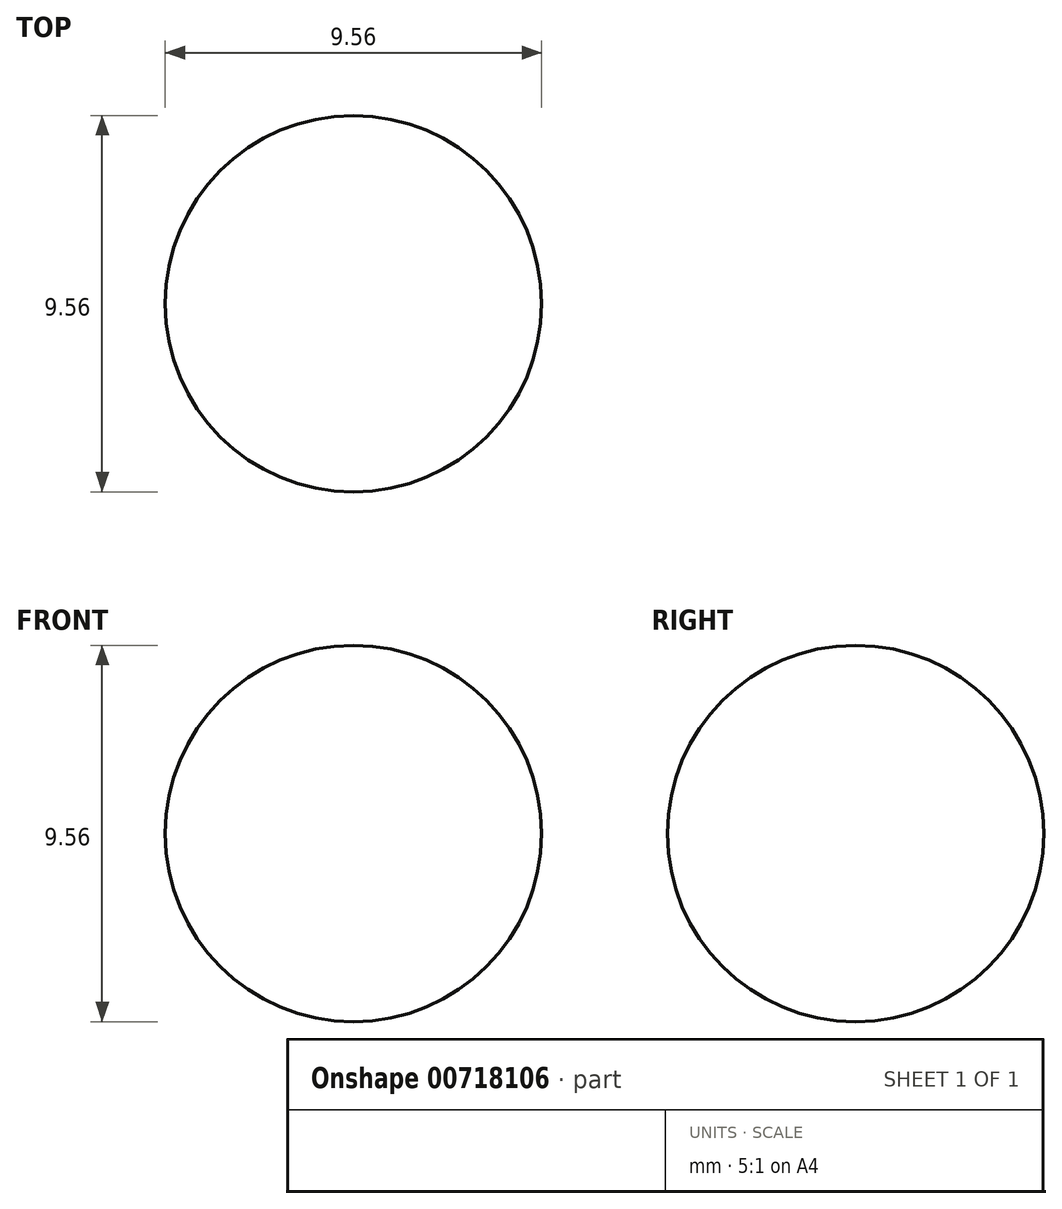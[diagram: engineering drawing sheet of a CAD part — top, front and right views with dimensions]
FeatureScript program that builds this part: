
annotation { "Feature Type Name" : "Feature", "Feature Type Description" : "" }
export const myFeature = defineFeature(function(context is Context, id is Id, definition is map)
    precondition{}
    {
        {
            var Q0;
            Q0=qCreatedBy(makeId("Top.planeOp"),FACE);
            var sketch = newSketch(context, id + "F0", { "sketchPlane" : qUnion([Q0])});
            skCircle(sketch, "E0", {"center": v(0, 0) * mm, "radius": 4.78 * mm});
            skLineSegment(sketch, "E1", {"start": v(0, 4.78) * mm, "end": v(0, -4.78) * mm});
            skSolve(sketch);
        }
        {
            var Q0;
            {var subQ0=sQuery(id+"F0.wireOp",EDGE,"E1");Q0=makeQuery(id+"F0.imprint","IMPRINT",FACE,{"disambiguationData":[TD([[makeQuery(id+"F0.imprint","IMPRINT",EDGE,{"derivedFrom":subQ0}),1.0]])]});}
            var Q1;
            Q1=sQuery(id+"F0.wireOp",EDGE,"E1");
            revolve(context, id + "F1", {"surfaceOperationType" : NewSurfaceOperationType.NEW, "entities" : qUnion([Q0]), "axis" : qUnion([Q1]), "revolveType" : RevolveType.FULL});
        }
    });
